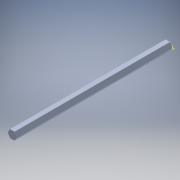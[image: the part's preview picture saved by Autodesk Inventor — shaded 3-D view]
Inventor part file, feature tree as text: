
AUTODESK INVENTOR PART (.ipt)
format: ipt  version: 2016 (Build 200138000, 138)  size: 141,824 bytes
history: native  units: in
note: dims shown in document units (in); Inventor stores cm internally (conversion verified against a paired STEP export)
features: sketch x2, fillet x1, other x1, extrude x1, imported_body x1
ambient origin geometry x8: Origin, YZ Plane, XZ Plane, XY Plane, X Axis, Y Axis, Z Axis, Center Point
bodies: Body1 (feature_tree)
feature tree (6):
  fillet  "Fillet1"  Radius=8.0in
  other  "18inShaft1"
  extrude  "Extrusion1"  [1 undecoded]
  sketch  "Sketch2"
  imported_body  "Base1"
  sketch  "Sketch1"
note: 1 required parameter value undecoded (feature->parameter linkage not recoverable at this tier; creation-order binding heuristic only, values carry confidence <= 0.55)
